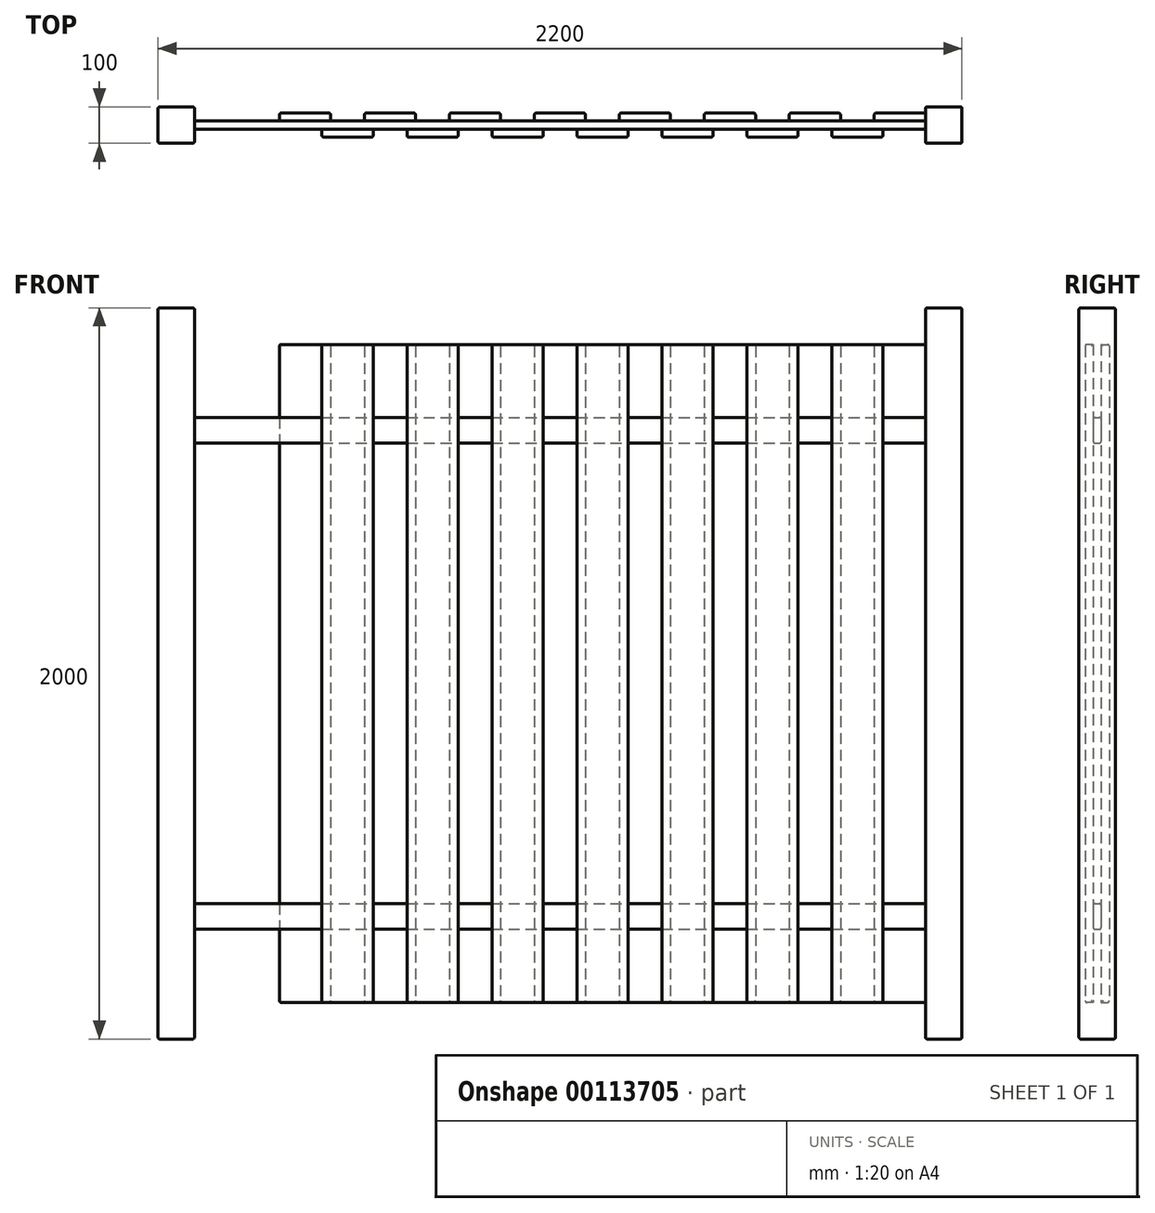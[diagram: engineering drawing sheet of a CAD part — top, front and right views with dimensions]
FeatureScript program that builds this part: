
annotation { "Feature Type Name" : "Feature", "Feature Type Description" : "" }
export const myFeature = defineFeature(function(context is Context, id is Id, definition is map)
    precondition{}
    {
        {
            var Q0;
            Q0=qCreatedBy(makeId("Top.planeOp"),FACE);
            var sketch = newSketch(context, id + "F0", { "sketchPlane" : qUnion([Q0])});
            skLineSegment(sketch, "E0.bottom", {"start": v(0, 0) * mm, "end": v(2000, 0) * mm});
            skLineSegment(sketch, "E0.top", {"start": v(0, 22) * mm, "end": v(2000, 22) * mm});
            skLineSegment(sketch, "E0.left", {"start": v(0, 0) * mm, "end": v(0, 22) * mm});
            skLineSegment(sketch, "E0.right", {"start": v(2000, 0) * mm, "end": v(2000, 22) * mm});
            skLineSegment(sketch, "E1.bottom", {"start": v(0, 22) * mm, "end": v(140, 22) * mm});
            skLineSegment(sketch, "E1.top", {"start": v(0, 44) * mm, "end": v(140, 44) * mm});
            skLineSegment(sketch, "E1.left", {"start": v(0, 22) * mm, "end": v(0, 44) * mm});
            skLineSegment(sketch, "E1.right", {"start": v(140, 22) * mm, "end": v(140, 44) * mm});
            skLineSegment(sketch, "E2.1.0.0", {"start": v(232.5, 44) * mm, "end": v(372.5, 44) * mm});
            skLineSegment(sketch, "E2.1.0.1", {"start": v(232.5, 22) * mm, "end": v(372.5, 22) * mm});
            skLineSegment(sketch, "E2.1.0.2", {"start": v(232.5, 22) * mm, "end": v(232.5, 44) * mm});
            skLineSegment(sketch, "E2.1.0.3", {"start": v(372.5, 22) * mm, "end": v(372.5, 44) * mm});
            skLineSegment(sketch, "E2.2.0.0", {"start": v(465, 44) * mm, "end": v(605, 44) * mm});
            skLineSegment(sketch, "E2.2.0.1", {"start": v(465, 22) * mm, "end": v(605, 22) * mm});
            skLineSegment(sketch, "E2.2.0.2", {"start": v(465, 22) * mm, "end": v(465, 44) * mm});
            skLineSegment(sketch, "E2.2.0.3", {"start": v(605, 22) * mm, "end": v(605, 44) * mm});
            skLineSegment(sketch, "E2.3.0.0", {"start": v(697.5, 44) * mm, "end": v(837.5, 44) * mm});
            skLineSegment(sketch, "E2.3.0.1", {"start": v(697.5, 22) * mm, "end": v(837.5, 22) * mm});
            skLineSegment(sketch, "E2.3.0.2", {"start": v(697.5, 22) * mm, "end": v(697.5, 44) * mm});
            skLineSegment(sketch, "E2.3.0.3", {"start": v(837.5, 22) * mm, "end": v(837.5, 44) * mm});
            skLineSegment(sketch, "E2.4.0.0", {"start": v(930, 44) * mm, "end": v(1070, 44) * mm});
            skLineSegment(sketch, "E2.4.0.1", {"start": v(930, 22) * mm, "end": v(1070, 22) * mm});
            skLineSegment(sketch, "E2.4.0.2", {"start": v(930, 22) * mm, "end": v(930, 44) * mm});
            skLineSegment(sketch, "E2.4.0.3", {"start": v(1070, 22) * mm, "end": v(1070, 44) * mm});
            skLineSegment(sketch, "E2.5.0.0", {"start": v(1162.5, 44) * mm, "end": v(1302.5, 44) * mm});
            skLineSegment(sketch, "E2.5.0.1", {"start": v(1162.5, 22) * mm, "end": v(1302.5, 22) * mm});
            skLineSegment(sketch, "E2.5.0.2", {"start": v(1162.5, 22) * mm, "end": v(1162.5, 44) * mm});
            skLineSegment(sketch, "E2.5.0.3", {"start": v(1302.5, 22) * mm, "end": v(1302.5, 44) * mm});
            skLineSegment(sketch, "E2.6.0.0", {"start": v(1395, 44) * mm, "end": v(1535, 44) * mm});
            skLineSegment(sketch, "E2.6.0.1", {"start": v(1395, 22) * mm, "end": v(1535, 22) * mm});
            skLineSegment(sketch, "E2.6.0.2", {"start": v(1395, 22) * mm, "end": v(1395, 44) * mm});
            skLineSegment(sketch, "E2.6.0.3", {"start": v(1535, 22) * mm, "end": v(1535, 44) * mm});
            skLineSegment(sketch, "E2.7.0.0", {"start": v(1627.5, 44) * mm, "end": v(1767.5, 44) * mm});
            skLineSegment(sketch, "E2.7.0.1", {"start": v(1627.5, 22) * mm, "end": v(1767.5, 22) * mm});
            skLineSegment(sketch, "E2.7.0.2", {"start": v(1627.5, 22) * mm, "end": v(1627.5, 44) * mm});
            skLineSegment(sketch, "E2.7.0.3", {"start": v(1767.5, 22) * mm, "end": v(1767.5, 44) * mm});
            skLineSegment(sketch, "E2.direction1", {"start": v(0, 22) * mm, "end": v(232.5, 22) * mm, "construction": true});
            skLineSegment(sketch, "E3.0.8.0", {"start": v(1860, 44) * mm, "end": v(2000, 44) * mm});
            skLineSegment(sketch, "E3.3.8.0", {"start": v(1860, 22) * mm, "end": v(2000, 22) * mm});
            skLineSegment(sketch, "E3.6.8.0", {"start": v(1860, 22) * mm, "end": v(1860, 44) * mm});
            skLineSegment(sketch, "E3.9.8.0", {"start": v(2000, 22) * mm, "end": v(2000, 44) * mm});
            skLineSegment(sketch, "E4.bottom", {"start": v(116.25, 0) * mm, "end": v(256.25, 0) * mm});
            skLineSegment(sketch, "E4.top", {"start": v(116.25, -22) * mm, "end": v(256.25, -22) * mm});
            skLineSegment(sketch, "E4.left", {"start": v(116.25, 0) * mm, "end": v(116.25, -22) * mm});
            skLineSegment(sketch, "E4.right", {"start": v(256.25, 0) * mm, "end": v(256.25, -22) * mm});
            skLineSegment(sketch, "E5.1.0.0", {"start": v(488.75, 0) * mm, "end": v(488.75, -22) * mm});
            skLineSegment(sketch, "E5.1.0.1", {"start": v(348.75, 0) * mm, "end": v(488.75, 0) * mm});
            skLineSegment(sketch, "E5.1.0.2", {"start": v(348.75, 0) * mm, "end": v(348.75, -22) * mm});
            skLineSegment(sketch, "E5.1.0.3", {"start": v(348.75, -22) * mm, "end": v(488.75, -22) * mm});
            skLineSegment(sketch, "E5.2.0.0", {"start": v(721.25, 0) * mm, "end": v(721.25, -22) * mm});
            skLineSegment(sketch, "E5.2.0.1", {"start": v(581.25, 0) * mm, "end": v(721.25, 0) * mm});
            skLineSegment(sketch, "E5.2.0.2", {"start": v(581.25, 0) * mm, "end": v(581.25, -22) * mm});
            skLineSegment(sketch, "E5.2.0.3", {"start": v(581.25, -22) * mm, "end": v(721.25, -22) * mm});
            skLineSegment(sketch, "E5.3.0.0", {"start": v(953.75, 0) * mm, "end": v(953.75, -22) * mm});
            skLineSegment(sketch, "E5.3.0.1", {"start": v(813.75, 0) * mm, "end": v(953.75, 0) * mm});
            skLineSegment(sketch, "E5.3.0.2", {"start": v(813.75, 0) * mm, "end": v(813.75, -22) * mm});
            skLineSegment(sketch, "E5.3.0.3", {"start": v(813.75, -22) * mm, "end": v(953.75, -22) * mm});
            skLineSegment(sketch, "E5.4.0.0", {"start": v(1186.25, 0) * mm, "end": v(1186.25, -22) * mm});
            skLineSegment(sketch, "E5.4.0.1", {"start": v(1046.25, 0) * mm, "end": v(1186.25, 0) * mm});
            skLineSegment(sketch, "E5.4.0.2", {"start": v(1046.25, 0) * mm, "end": v(1046.25, -22) * mm});
            skLineSegment(sketch, "E5.4.0.3", {"start": v(1046.25, -22) * mm, "end": v(1186.25, -22) * mm});
            skLineSegment(sketch, "E5.5.0.0", {"start": v(1418.75, 0) * mm, "end": v(1418.75, -22) * mm});
            skLineSegment(sketch, "E5.5.0.1", {"start": v(1278.75, 0) * mm, "end": v(1418.75, 0) * mm});
            skLineSegment(sketch, "E5.5.0.2", {"start": v(1278.75, 0) * mm, "end": v(1278.75, -22) * mm});
            skLineSegment(sketch, "E5.5.0.3", {"start": v(1278.75, -22) * mm, "end": v(1418.75, -22) * mm});
            skLineSegment(sketch, "E5.6.0.0", {"start": v(1651.25, 0) * mm, "end": v(1651.25, -22) * mm});
            skLineSegment(sketch, "E5.6.0.1", {"start": v(1511.25, 0) * mm, "end": v(1651.25, 0) * mm});
            skLineSegment(sketch, "E5.6.0.2", {"start": v(1511.25, 0) * mm, "end": v(1511.25, -22) * mm});
            skLineSegment(sketch, "E5.6.0.3", {"start": v(1511.25, -22) * mm, "end": v(1651.25, -22) * mm});
            skLineSegment(sketch, "E5.7.0.0", {"start": v(1883.75, 0) * mm, "end": v(1883.75, -22) * mm});
            skLineSegment(sketch, "E5.7.0.1", {"start": v(1743.75, 0) * mm, "end": v(1883.75, 0) * mm});
            skLineSegment(sketch, "E5.7.0.2", {"start": v(1743.75, 0) * mm, "end": v(1743.75, -22) * mm});
            skLineSegment(sketch, "E5.7.0.3", {"start": v(1743.75, -22) * mm, "end": v(1883.75, -22) * mm});
            skLineSegment(sketch, "E5.direction1", {"start": v(116.25, -22) * mm, "end": v(348.75, -22) * mm, "construction": true});
            skSolve(sketch);
        }
        {
            var Q0;
            Q0=makeQuery(id+"F0.imprint","IMPRINT",FACE,{"disambiguationData":[TD([[makeQuery(id+"F0.imprint","IMPRINT",EDGE,{"derivedFrom":sQuery(id+"F0.wireOp",EDGE,"E1.bottom")}),1.0]])]});
            var Q1;
            Q1=makeQuery(id+"F0.imprint","IMPRINT",FACE,{"disambiguationData":[TD([[makeQuery(id+"F0.imprint","IMPRINT",EDGE,{"derivedFrom":sQuery(id+"F0.wireOp",EDGE,"E2.1.0.0")}),-1.0]])]});
            var Q2;
            Q2=makeQuery(id+"F0.imprint","IMPRINT",FACE,{"disambiguationData":[TD([[makeQuery(id+"F0.imprint","IMPRINT",EDGE,{"derivedFrom":sQuery(id+"F0.wireOp",EDGE,"E2.2.0.0")}),-1.0]])]});
            var Q3;
            Q3=makeQuery(id+"F0.imprint","IMPRINT",FACE,{"disambiguationData":[TD([[makeQuery(id+"F0.imprint","IMPRINT",EDGE,{"derivedFrom":sQuery(id+"F0.wireOp",EDGE,"E2.3.0.0")}),-1.0]])]});
            var Q4;
            Q4=makeQuery(id+"F0.imprint","IMPRINT",FACE,{"disambiguationData":[TD([[makeQuery(id+"F0.imprint","IMPRINT",EDGE,{"derivedFrom":sQuery(id+"F0.wireOp",EDGE,"E2.4.0.0")}),-1.0]])]});
            var Q5;
            Q5=makeQuery(id+"F0.imprint","IMPRINT",FACE,{"disambiguationData":[TD([[makeQuery(id+"F0.imprint","IMPRINT",EDGE,{"derivedFrom":sQuery(id+"F0.wireOp",EDGE,"E2.5.0.0")}),-1.0]])]});
            var Q6;
            Q6=makeQuery(id+"F0.imprint","IMPRINT",FACE,{"disambiguationData":[TD([[makeQuery(id+"F0.imprint","IMPRINT",EDGE,{"derivedFrom":sQuery(id+"F0.wireOp",EDGE,"E2.6.0.0")}),-1.0]])]});
            var Q7;
            Q7=makeQuery(id+"F0.imprint","IMPRINT",FACE,{"disambiguationData":[TD([[makeQuery(id+"F0.imprint","IMPRINT",EDGE,{"derivedFrom":sQuery(id+"F0.wireOp",EDGE,"E2.7.0.0")}),-1.0]])]});
            var Q8;
            Q8=makeQuery(id+"F0.imprint","IMPRINT",FACE,{"disambiguationData":[TD([[makeQuery(id+"F0.imprint","IMPRINT",EDGE,{"derivedFrom":sQuery(id+"F0.wireOp",EDGE,"E3.0.8.0")}),-1.0]])]});
            var Q9;
            Q9=makeQuery(id+"F0.imprint","IMPRINT",FACE,{"disambiguationData":[TD([[makeQuery(id+"F0.imprint","IMPRINT",EDGE,{"derivedFrom":sQuery(id+"F0.wireOp",EDGE,"E5.7.0.0")}),-1.0]])]});
            var Q10;
            Q10=makeQuery(id+"F0.imprint","IMPRINT",FACE,{"disambiguationData":[TD([[makeQuery(id+"F0.imprint","IMPRINT",EDGE,{"derivedFrom":sQuery(id+"F0.wireOp",EDGE,"E5.6.0.0")}),-1.0]])]});
            var Q11;
            Q11=makeQuery(id+"F0.imprint","IMPRINT",FACE,{"disambiguationData":[TD([[makeQuery(id+"F0.imprint","IMPRINT",EDGE,{"derivedFrom":sQuery(id+"F0.wireOp",EDGE,"E5.5.0.0")}),-1.0]])]});
            var Q12;
            Q12=makeQuery(id+"F0.imprint","IMPRINT",FACE,{"disambiguationData":[TD([[makeQuery(id+"F0.imprint","IMPRINT",EDGE,{"derivedFrom":sQuery(id+"F0.wireOp",EDGE,"E5.4.0.0")}),-1.0]])]});
            var Q13;
            Q13=makeQuery(id+"F0.imprint","IMPRINT",FACE,{"disambiguationData":[TD([[makeQuery(id+"F0.imprint","IMPRINT",EDGE,{"derivedFrom":sQuery(id+"F0.wireOp",EDGE,"E5.3.0.0")}),-1.0]])]});
            var Q14;
            Q14=makeQuery(id+"F0.imprint","IMPRINT",FACE,{"disambiguationData":[TD([[makeQuery(id+"F0.imprint","IMPRINT",EDGE,{"derivedFrom":sQuery(id+"F0.wireOp",EDGE,"E5.2.0.0")}),-1.0]])]});
            var Q15;
            Q15=makeQuery(id+"F0.imprint","IMPRINT",FACE,{"disambiguationData":[TD([[makeQuery(id+"F0.imprint","IMPRINT",EDGE,{"derivedFrom":sQuery(id+"F0.wireOp",EDGE,"E5.1.0.0")}),-1.0]])]});
            var Q16;
            Q16=makeQuery(id+"F0.imprint","IMPRINT",FACE,{"disambiguationData":[TD([[makeQuery(id+"F0.imprint","IMPRINT",EDGE,{"derivedFrom":sQuery(id+"F0.wireOp",EDGE,"E4.bottom")}),-1.0]])]});
            extrude(context, id + "F1", {"entities" : qUnion([Q0, Q1, Q2, Q3, Q4, Q5, Q6, Q7, Q8, Q9, Q10, Q11, Q12, Q13, Q14, Q15, Q16]), "depth" : 1800 * mm});
        }
        {
            var Q0;
            Q0=makeQuery(id+"F1.opExtrude","SWEPT_FACE",FACE,{"disambiguationData":[OSD([sQuery(id+"F0.wireOp",EDGE,"E3.9.8.0")])]});
            var sketch = newSketch(context, id + "F2", { "sketchPlane" : qUnion([Q0])});
            skLineSegment(sketch, "E6.bottom", {"start": v(0, 270) * mm, "end": v(22, 270) * mm});
            skLineSegment(sketch, "E6.top", {"start": v(0, 200) * mm, "end": v(22, 200) * mm});
            skLineSegment(sketch, "E6.left", {"start": v(0, 270) * mm, "end": v(0, 200) * mm});
            skLineSegment(sketch, "E6.right", {"start": v(22, 270) * mm, "end": v(22, 200) * mm});
            skLineSegment(sketch, "E7.bottom", {"start": v(0, 1600) * mm, "end": v(22, 1600) * mm});
            skLineSegment(sketch, "E7.top", {"start": v(0, 1530) * mm, "end": v(22, 1530) * mm});
            skLineSegment(sketch, "E7.left", {"start": v(0, 1600) * mm, "end": v(0, 1530) * mm});
            skLineSegment(sketch, "E7.right", {"start": v(22, 1600) * mm, "end": v(22, 1530) * mm});
            skSolve(sketch);
        }
        {
            var Q0;
            Q0 = qSketchRegion(id + "F2", true);
            extrude(context, id + "F3", {"entities" : qUnion([Q0]), "oppositeDirection" : true, "depth" : 2000 * mm});
        }
        {
            var Q0;
            Q0=qCreatedBy(makeId("Top.planeOp"),FACE);
            var sketch = newSketch(context, id + "F4", { "sketchPlane" : qUnion([Q0])});
            skLineSegment(sketch, "E8.bottom", {"start": v(-100, 61) * mm, "end": v(0, 61) * mm});
            skLineSegment(sketch, "E8.top", {"start": v(-100, -39) * mm, "end": v(0, -39) * mm});
            skLineSegment(sketch, "E8.left", {"start": v(-100, 61) * mm, "end": v(-100, -39) * mm});
            skLineSegment(sketch, "E8.right", {"start": v(0, 61) * mm, "end": v(0, -39) * mm});
            skLineSegment(sketch, "E9.bottom", {"start": v(2000, 61) * mm, "end": v(2100, 61) * mm});
            skLineSegment(sketch, "E9.top", {"start": v(2000, -39) * mm, "end": v(2100, -39) * mm});
            skLineSegment(sketch, "E9.left", {"start": v(2000, 61) * mm, "end": v(2000, -39) * mm});
            skLineSegment(sketch, "E9.right", {"start": v(2100, 61) * mm, "end": v(2100, -39) * mm});
            skSolve(sketch);
        }
        {
            var Q0;
            Q0=makeQuery(id+"F4.imprint","IMPRINT",FACE,{"disambiguationData":[TD([[makeQuery(id+"F4.imprint","IMPRINT",EDGE,{"derivedFrom":sQuery(id+"F4.wireOp",EDGE,"E8.bottom")}),-1.0]])]});
            var Q1;
            Q1=makeQuery(id+"F4.imprint","IMPRINT",FACE,{"disambiguationData":[TD([[makeQuery(id+"F4.imprint","IMPRINT",EDGE,{"derivedFrom":sQuery(id+"F4.wireOp",EDGE,"E9.bottom")}),-1.0]])]});
            extrude(context, id + "F5", {"entities" : qUnion([Q0, Q1]), "depth" : 1900 * mm, "hasSecondDirection" : true, "secondDirectionOppositeDirection" : true, "secondDirectionDepth" : 100 * mm});
        }
        {
            var Q0;
            Q0=makeQuery(id+"F5.opExtrude","SWEPT_FACE",FACE,{"disambiguationData":[OSD([sQuery(id+"F4.wireOp",EDGE,"E8.top")])]});
            var Q1;
            Q1=makeQuery(id+"F1.opExtrude","SWEPT_EDGE",EDGE,{"disambiguationData":[OSD([sQuery(id+"F0.wireOp",EDGE,"E0.left"),sQuery(id+"F0.wireOp",EDGE,"E1.bottom"),sQuery(id+"F0.wireOp",EDGE,"E1.left")])]});
            var Q2;
            Q2=makeQuery(id+"F1.opExtrude","SWEPT_EDGE",EDGE,{"disambiguationData":[OSD([sQuery(id+"F0.wireOp",EDGE,"E4.top"),sQuery(id+"F0.wireOp",EDGE,"E4.right")])]});
            var Q3;
            Q3=makeQuery(id+"F1.opExtrude","SWEPT_EDGE",EDGE,{"disambiguationData":[OSD([sQuery(id+"F0.wireOp",EDGE,"E4.top"),sQuery(id+"F0.wireOp",EDGE,"E4.left")])]});
            var Q4;
            Q4=makeQuery(id+"F1.opExtrude","SWEPT_EDGE",EDGE,{"disambiguationData":[OSD([sQuery(id+"F0.wireOp",EDGE,"E0.bottom"),sQuery(id+"F0.wireOp",EDGE,"E4.bottom"),sQuery(id+"F0.wireOp",EDGE,"E4.right")])]});
            var Q5;
            Q5=makeQuery(id+"F1.opExtrude","SWEPT_EDGE",EDGE,{"disambiguationData":[OSD([sQuery(id+"F0.wireOp",EDGE,"E5.1.0.2"),sQuery(id+"F0.wireOp",EDGE,"E5.1.0.3")])]});
            var Q6;
            Q6=makeQuery(id+"F1.opExtrude","SWEPT_EDGE",EDGE,{"disambiguationData":[OSD([sQuery(id+"F0.wireOp",EDGE,"E0.bottom"),sQuery(id+"F0.wireOp",EDGE,"E5.1.0.0"),sQuery(id+"F0.wireOp",EDGE,"E5.1.0.1")])]});
            var Q7;
            Q7=makeQuery(id+"F1.opExtrude","SWEPT_EDGE",EDGE,{"disambiguationData":[OSD([sQuery(id+"F0.wireOp",EDGE,"E5.1.0.0"),sQuery(id+"F0.wireOp",EDGE,"E5.1.0.3")])]});
            var Q8;
            Q8=makeQuery(id+"F1.opExtrude","SWEPT_EDGE",EDGE,{"disambiguationData":[OSD([sQuery(id+"F0.wireOp",EDGE,"E5.2.0.2"),sQuery(id+"F0.wireOp",EDGE,"E5.2.0.3")])]});
            var Q9;
            Q9=makeQuery(id+"F1.opExtrude","SWEPT_EDGE",EDGE,{"disambiguationData":[OSD([sQuery(id+"F0.wireOp",EDGE,"E0.bottom"),sQuery(id+"F0.wireOp",EDGE,"E5.2.0.0"),sQuery(id+"F0.wireOp",EDGE,"E5.2.0.1")])]});
            var Q10;
            Q10=makeQuery(id+"F1.opExtrude","SWEPT_EDGE",EDGE,{"disambiguationData":[OSD([sQuery(id+"F0.wireOp",EDGE,"E5.2.0.0"),sQuery(id+"F0.wireOp",EDGE,"E5.2.0.3")])]});
            var Q11;
            Q11=makeQuery(id+"F1.opExtrude","CAP_EDGE",EDGE,{"disambiguationData":[OSD([sQuery(id+"F0.wireOp",EDGE,"E5.2.0.3")])],"isStart":true});
            var Q12;
            Q12=makeQuery(id+"F1.opExtrude","SWEPT_EDGE",EDGE,{"disambiguationData":[OSD([sQuery(id+"F0.wireOp",EDGE,"E0.bottom"),sQuery(id+"F0.wireOp",EDGE,"E5.3.0.0"),sQuery(id+"F0.wireOp",EDGE,"E5.3.0.1")])]});
            var Q13;
            Q13=makeQuery(id+"F1.opExtrude","CAP_EDGE",EDGE,{"disambiguationData":[OSD([sQuery(id+"F0.wireOp",EDGE,"E5.3.0.3")])],"isStart":false});
            var Q14;
            Q14=makeQuery(id+"F1.opExtrude","SWEPT_EDGE",EDGE,{"disambiguationData":[OSD([sQuery(id+"F0.wireOp",EDGE,"E5.3.0.0"),sQuery(id+"F0.wireOp",EDGE,"E5.3.0.3")])]});
            var Q15;
            Q15=makeQuery(id+"F1.opExtrude","SWEPT_EDGE",EDGE,{"disambiguationData":[OSD([sQuery(id+"F0.wireOp",EDGE,"E5.3.0.2"),sQuery(id+"F0.wireOp",EDGE,"E5.3.0.3")])]});
            var Q16;
            Q16=makeQuery(id+"F1.opExtrude","SWEPT_EDGE",EDGE,{"disambiguationData":[OSD([sQuery(id+"F0.wireOp",EDGE,"E5.4.0.2"),sQuery(id+"F0.wireOp",EDGE,"E5.4.0.3")])]});
            var Q17;
            Q17=makeQuery(id+"F1.opExtrude","SWEPT_EDGE",EDGE,{"disambiguationData":[OSD([sQuery(id+"F0.wireOp",EDGE,"E5.4.0.0"),sQuery(id+"F0.wireOp",EDGE,"E5.4.0.3")])]});
            var Q18;
            Q18=makeQuery(id+"F1.opExtrude","SWEPT_EDGE",EDGE,{"disambiguationData":[OSD([sQuery(id+"F0.wireOp",EDGE,"E0.bottom"),sQuery(id+"F0.wireOp",EDGE,"E5.4.0.0"),sQuery(id+"F0.wireOp",EDGE,"E5.4.0.1")])]});
            var Q19;
            Q19=makeQuery(id+"F1.opExtrude","CAP_EDGE",EDGE,{"disambiguationData":[OSD([sQuery(id+"F0.wireOp",EDGE,"E5.5.0.3")])],"isStart":false});
            var Q20;
            Q20=makeQuery(id+"F1.opExtrude","SWEPT_EDGE",EDGE,{"disambiguationData":[OSD([sQuery(id+"F0.wireOp",EDGE,"E5.5.0.2"),sQuery(id+"F0.wireOp",EDGE,"E5.5.0.3")])]});
            var Q21;
            Q21=makeQuery(id+"F1.opExtrude","SWEPT_EDGE",EDGE,{"disambiguationData":[OSD([sQuery(id+"F0.wireOp",EDGE,"E0.bottom"),sQuery(id+"F0.wireOp",EDGE,"E5.5.0.0"),sQuery(id+"F0.wireOp",EDGE,"E5.5.0.1")])]});
            var Q22;
            Q22=makeQuery(id+"F1.opExtrude","SWEPT_EDGE",EDGE,{"disambiguationData":[OSD([sQuery(id+"F0.wireOp",EDGE,"E5.5.0.0"),sQuery(id+"F0.wireOp",EDGE,"E5.5.0.3")])]});
            var Q23;
            Q23=makeQuery(id+"F1.opExtrude","CAP_EDGE",EDGE,{"disambiguationData":[OSD([sQuery(id+"F0.wireOp",EDGE,"E5.5.0.3")])],"isStart":true});
            var Q24;
            Q24=makeQuery(id+"F1.opExtrude","SWEPT_EDGE",EDGE,{"disambiguationData":[OSD([sQuery(id+"F0.wireOp",EDGE,"E5.6.0.2"),sQuery(id+"F0.wireOp",EDGE,"E5.6.0.3")])]});
            var Q25;
            Q25=makeQuery(id+"F1.opExtrude","SWEPT_EDGE",EDGE,{"disambiguationData":[OSD([sQuery(id+"F0.wireOp",EDGE,"E0.bottom"),sQuery(id+"F0.wireOp",EDGE,"E5.6.0.0"),sQuery(id+"F0.wireOp",EDGE,"E5.6.0.1")])]});
            var Q26;
            Q26=makeQuery(id+"F1.opExtrude","SWEPT_EDGE",EDGE,{"disambiguationData":[OSD([sQuery(id+"F0.wireOp",EDGE,"E5.6.0.0"),sQuery(id+"F0.wireOp",EDGE,"E5.6.0.3")])]});
            var Q27;
            Q27=makeQuery(id+"F1.opExtrude","SWEPT_EDGE",EDGE,{"disambiguationData":[OSD([sQuery(id+"F0.wireOp",EDGE,"E0.bottom"),sQuery(id+"F0.wireOp",EDGE,"E5.7.0.0"),sQuery(id+"F0.wireOp",EDGE,"E5.7.0.1")])]});
            var Q28;
            Q28=makeQuery(id+"F1.opExtrude","CAP_EDGE",EDGE,{"disambiguationData":[OSD([sQuery(id+"F0.wireOp",EDGE,"E5.7.0.3")])],"isStart":false});
            var Q29;
            Q29=makeQuery(id+"F1.opExtrude","SWEPT_EDGE",EDGE,{"disambiguationData":[OSD([sQuery(id+"F0.wireOp",EDGE,"E5.7.0.0"),sQuery(id+"F0.wireOp",EDGE,"E5.7.0.3")])]});
            var Q30;
            Q30=makeQuery(id+"F1.opExtrude","CAP_EDGE",EDGE,{"disambiguationData":[OSD([sQuery(id+"F0.wireOp",EDGE,"E5.7.0.3")])],"isStart":true});
            var Q31;
            Q31=makeQuery(id+"F1.opExtrude","SWEPT_EDGE",EDGE,{"disambiguationData":[OSD([sQuery(id+"F0.wireOp",EDGE,"E5.7.0.2"),sQuery(id+"F0.wireOp",EDGE,"E5.7.0.3")])]});
            var Q32;
            Q32=makeQuery(id+"F3.opExtrude","SWEPT_EDGE",EDGE,{"disambiguationData":[OSD([sQuery(id+"F2.wireOp",EDGE,"E6.top"),sQuery(id+"F2.wireOp",EDGE,"E6.left")])]});
            var Q33;
            Q33=makeQuery(id+"F3.opExtrude","SWEPT_EDGE",EDGE,{"disambiguationData":[OSD([sQuery(id+"F0.wireOp",EDGE,"E0.right"),sQuery(id+"F0.wireOp",EDGE,"E3.3.8.0"),sQuery(id+"F0.wireOp",EDGE,"E3.9.8.0"),sQuery(id+"F2.wireOp",EDGE,"E6.bottom"),sQuery(id+"F2.wireOp",EDGE,"E6.right")])]});
            var Q34;
            Q34=makeQuery(id+"F3.opExtrude","SWEPT_EDGE",EDGE,{"disambiguationData":[OSD([sQuery(id+"F2.wireOp",EDGE,"E6.bottom"),sQuery(id+"F2.wireOp",EDGE,"E6.left")])]});
            var Q35;
            Q35=makeQuery(id+"F3.opExtrude","SWEPT_EDGE",EDGE,{"disambiguationData":[OSD([sQuery(id+"F2.wireOp",EDGE,"E7.top"),sQuery(id+"F2.wireOp",EDGE,"E7.left")])]});
            var Q36;
            Q36=makeQuery(id+"F3.opExtrude","SWEPT_EDGE",EDGE,{"disambiguationData":[OSD([sQuery(id+"F0.wireOp",EDGE,"E0.right"),sQuery(id+"F0.wireOp",EDGE,"E3.3.8.0"),sQuery(id+"F0.wireOp",EDGE,"E3.9.8.0"),sQuery(id+"F2.wireOp",EDGE,"E7.bottom"),sQuery(id+"F2.wireOp",EDGE,"E7.right")])]});
            var Q37;
            Q37=makeQuery(id+"F3.opExtrude","SWEPT_EDGE",EDGE,{"disambiguationData":[OSD([sQuery(id+"F2.wireOp",EDGE,"E7.bottom"),sQuery(id+"F2.wireOp",EDGE,"E7.left")])]});
            var Q38;
            Q38=makeQuery(id+"F5.opExtrude","CAP_EDGE",EDGE,{"disambiguationData":[OSD([sQuery(id+"F4.wireOp",EDGE,"E8.top")])],"isStart":false});
            var Q39;
            Q39=makeQuery(id+"F5.opExtrude","SWEPT_EDGE",EDGE,{"disambiguationData":[OSD([sQuery(id+"F4.wireOp",EDGE,"E8.top"),sQuery(id+"F4.wireOp",EDGE,"E8.right")])]});
            var Q40;
            Q40=makeQuery(id+"F5.opExtrude","SWEPT_EDGE",EDGE,{"disambiguationData":[OSD([sQuery(id+"F4.wireOp",EDGE,"E8.top"),sQuery(id+"F4.wireOp",EDGE,"E8.left")])]});
            var Q41;
            Q41=makeQuery(id+"F5.opExtrude","SWEPT_EDGE",EDGE,{"disambiguationData":[OSD([sQuery(id+"F4.wireOp",EDGE,"E9.top"),sQuery(id+"F4.wireOp",EDGE,"E9.right")])]});
            var Q42;
            Q42=makeQuery(id+"F5.opExtrude","SWEPT_EDGE",EDGE,{"disambiguationData":[OSD([sQuery(id+"F4.wireOp",EDGE,"E9.top"),sQuery(id+"F4.wireOp",EDGE,"E9.left")])]});
            var Q43;
            Q43=makeQuery(id+"F5.opExtrude","SWEPT_EDGE",EDGE,{"disambiguationData":[OSD([sQuery(id+"F4.wireOp",EDGE,"E9.bottom"),sQuery(id+"F4.wireOp",EDGE,"E9.right")])]});
            var Q44;
            Q44=makeQuery(id+"F1.opExtrude","CAP_EDGE",EDGE,{"disambiguationData":[OSD([sQuery(id+"F0.wireOp",EDGE,"E1.bottom")])],"isStart":false});
            var Q45;
            Q45=makeQuery(id+"F1.opExtrude","SWEPT_EDGE",EDGE,{"disambiguationData":[OSD([sQuery(id+"F0.wireOp",EDGE,"E1.top"),sQuery(id+"F0.wireOp",EDGE,"E1.left")])]});
            var Q46;
            Q46=makeQuery(id+"F1.opExtrude","CAP_EDGE",EDGE,{"disambiguationData":[OSD([sQuery(id+"F0.wireOp",EDGE,"E2.5.0.1")])],"isStart":true});
            var Q47;
            Q47=makeQuery(id+"F1.opExtrude","CAP_EDGE",EDGE,{"disambiguationData":[OSD([sQuery(id+"F0.wireOp",EDGE,"E2.7.0.1")])],"isStart":true});
            var Q48;
            Q48=makeQuery(id+"F1.opExtrude","CAP_EDGE",EDGE,{"disambiguationData":[OSD([sQuery(id+"F0.wireOp",EDGE,"E3.3.8.0")])],"isStart":true});
            var Q49;
            Q49=makeQuery(id+"F1.opExtrude","CAP_EDGE",EDGE,{"disambiguationData":[OSD([sQuery(id+"F0.wireOp",EDGE,"E3.3.8.0")])],"isStart":false});
            var Q50;
            Q50=makeQuery(id+"F1.opExtrude","CAP_EDGE",EDGE,{"disambiguationData":[OSD([sQuery(id+"F0.wireOp",EDGE,"E3.9.8.0")])],"isStart":false});
            var Q51;
            Q51=makeQuery(id+"F1.opExtrude","SWEPT_EDGE",EDGE,{"disambiguationData":[OSD([sQuery(id+"F0.wireOp",EDGE,"E0.right"),sQuery(id+"F0.wireOp",EDGE,"E3.3.8.0"),sQuery(id+"F0.wireOp",EDGE,"E3.9.8.0")])]});
            var Q52;
            Q52=makeQuery(id+"F1.opExtrude","SWEPT_EDGE",EDGE,{"disambiguationData":[OSD([sQuery(id+"F0.wireOp",EDGE,"E3.0.8.0"),sQuery(id+"F0.wireOp",EDGE,"E3.9.8.0")])]});
            var Q53;
            Q53=makeQuery(id+"F1.opExtrude","CAP_EDGE",EDGE,{"disambiguationData":[OSD([sQuery(id+"F0.wireOp",EDGE,"E4.top")])],"isStart":true});
            var Q54;
            Q54=makeQuery(id+"F1.opExtrude","CAP_EDGE",EDGE,{"disambiguationData":[OSD([sQuery(id+"F0.wireOp",EDGE,"E4.top")])],"isStart":false});
            var Q55;
            Q55=makeQuery(id+"F1.opExtrude","SWEPT_EDGE",EDGE,{"disambiguationData":[OSD([sQuery(id+"F0.wireOp",EDGE,"E0.bottom"),sQuery(id+"F0.wireOp",EDGE,"E4.bottom"),sQuery(id+"F0.wireOp",EDGE,"E4.left")])]});
            var Q56;
            Q56=makeQuery(id+"F1.opExtrude","CAP_EDGE",EDGE,{"disambiguationData":[OSD([sQuery(id+"F0.wireOp",EDGE,"E5.1.0.0")])],"isStart":true});
            var Q57;
            Q57=makeQuery(id+"F1.opExtrude","CAP_EDGE",EDGE,{"disambiguationData":[OSD([sQuery(id+"F0.wireOp",EDGE,"E5.1.0.3")])],"isStart":false});
            var Q58;
            Q58=makeQuery(id+"F1.opExtrude","CAP_EDGE",EDGE,{"disambiguationData":[OSD([sQuery(id+"F0.wireOp",EDGE,"E5.1.0.2")])],"isStart":true});
            var Q59;
            Q59=makeQuery(id+"F1.opExtrude","SWEPT_EDGE",EDGE,{"disambiguationData":[OSD([sQuery(id+"F0.wireOp",EDGE,"E0.bottom"),sQuery(id+"F0.wireOp",EDGE,"E5.1.0.1"),sQuery(id+"F0.wireOp",EDGE,"E5.1.0.2")])]});
            var Q60;
            Q60=makeQuery(id+"F1.opExtrude","CAP_EDGE",EDGE,{"disambiguationData":[OSD([sQuery(id+"F0.wireOp",EDGE,"E5.1.0.3")])],"isStart":true});
            var Q61;
            Q61=makeQuery(id+"F1.opExtrude","CAP_EDGE",EDGE,{"disambiguationData":[OSD([sQuery(id+"F0.wireOp",EDGE,"E5.2.0.1")])],"isStart":false});
            var Q62;
            Q62=makeQuery(id+"F1.opExtrude","SWEPT_EDGE",EDGE,{"disambiguationData":[OSD([sQuery(id+"F0.wireOp",EDGE,"E0.bottom"),sQuery(id+"F0.wireOp",EDGE,"E5.2.0.1"),sQuery(id+"F0.wireOp",EDGE,"E5.2.0.2")])]});
            var Q63;
            Q63=makeQuery(id+"F1.opExtrude","CAP_EDGE",EDGE,{"disambiguationData":[OSD([sQuery(id+"F0.wireOp",EDGE,"E5.2.0.2")])],"isStart":true});
            var Q64;
            Q64=makeQuery(id+"F1.opExtrude","CAP_EDGE",EDGE,{"disambiguationData":[OSD([sQuery(id+"F0.wireOp",EDGE,"E5.2.0.0")])],"isStart":true});
            var Q65;
            Q65=makeQuery(id+"F1.opExtrude","CAP_EDGE",EDGE,{"disambiguationData":[OSD([sQuery(id+"F0.wireOp",EDGE,"E5.2.0.0")])],"isStart":false});
            var Q66;
            Q66=makeQuery(id+"F1.opExtrude","CAP_EDGE",EDGE,{"disambiguationData":[OSD([sQuery(id+"F0.wireOp",EDGE,"E5.2.0.2")])],"isStart":false});
            var Q67;
            Q67=makeQuery(id+"F1.opExtrude","CAP_EDGE",EDGE,{"disambiguationData":[OSD([sQuery(id+"F0.wireOp",EDGE,"E5.2.0.3")])],"isStart":false});
            var Q68;
            Q68=makeQuery(id+"F1.opExtrude","CAP_EDGE",EDGE,{"disambiguationData":[OSD([sQuery(id+"F0.wireOp",EDGE,"E5.3.0.0")])],"isStart":false});
            var Q69;
            Q69=makeQuery(id+"F1.opExtrude","CAP_EDGE",EDGE,{"disambiguationData":[OSD([sQuery(id+"F0.wireOp",EDGE,"E5.3.0.1")])],"isStart":true});
            var Q70;
            Q70=makeQuery(id+"F1.opExtrude","CAP_EDGE",EDGE,{"disambiguationData":[OSD([sQuery(id+"F0.wireOp",EDGE,"E5.3.0.0")])],"isStart":true});
            var Q71;
            Q71=makeQuery(id+"F1.opExtrude","CAP_EDGE",EDGE,{"disambiguationData":[OSD([sQuery(id+"F0.wireOp",EDGE,"E5.3.0.2")])],"isStart":true});
            var Q72;
            Q72=makeQuery(id+"F1.opExtrude","CAP_EDGE",EDGE,{"disambiguationData":[OSD([sQuery(id+"F0.wireOp",EDGE,"E5.3.0.2")])],"isStart":false});
            var Q73;
            Q73=makeQuery(id+"F1.opExtrude","SWEPT_EDGE",EDGE,{"disambiguationData":[OSD([sQuery(id+"F0.wireOp",EDGE,"E0.bottom"),sQuery(id+"F0.wireOp",EDGE,"E5.3.0.1"),sQuery(id+"F0.wireOp",EDGE,"E5.3.0.2")])]});
            var Q74;
            Q74=makeQuery(id+"F1.opExtrude","CAP_EDGE",EDGE,{"disambiguationData":[OSD([sQuery(id+"F0.wireOp",EDGE,"E5.3.0.3")])],"isStart":true});
            var Q75;
            Q75=makeQuery(id+"F1.opExtrude","CAP_EDGE",EDGE,{"disambiguationData":[OSD([sQuery(id+"F0.wireOp",EDGE,"E5.4.0.1")])],"isStart":true});
            var Q76;
            Q76=makeQuery(id+"F1.opExtrude","SWEPT_EDGE",EDGE,{"disambiguationData":[OSD([sQuery(id+"F0.wireOp",EDGE,"E0.bottom"),sQuery(id+"F0.wireOp",EDGE,"E5.4.0.1"),sQuery(id+"F0.wireOp",EDGE,"E5.4.0.2")])]});
            var Q77;
            Q77=makeQuery(id+"F1.opExtrude","CAP_EDGE",EDGE,{"disambiguationData":[OSD([sQuery(id+"F0.wireOp",EDGE,"E5.4.0.0")])],"isStart":true});
            var Q78;
            Q78=makeQuery(id+"F1.opExtrude","CAP_EDGE",EDGE,{"disambiguationData":[OSD([sQuery(id+"F0.wireOp",EDGE,"E5.4.0.1")])],"isStart":false});
            var Q79;
            Q79=makeQuery(id+"F1.opExtrude","CAP_EDGE",EDGE,{"disambiguationData":[OSD([sQuery(id+"F0.wireOp",EDGE,"E5.4.0.2")])],"isStart":true});
            var Q80;
            Q80=makeQuery(id+"F1.opExtrude","CAP_EDGE",EDGE,{"disambiguationData":[OSD([sQuery(id+"F0.wireOp",EDGE,"E5.4.0.0")])],"isStart":false});
            var Q81;
            Q81=makeQuery(id+"F1.opExtrude","CAP_EDGE",EDGE,{"disambiguationData":[OSD([sQuery(id+"F0.wireOp",EDGE,"E5.4.0.2")])],"isStart":false});
            var Q82;
            Q82=makeQuery(id+"F1.opExtrude","CAP_EDGE",EDGE,{"disambiguationData":[OSD([sQuery(id+"F0.wireOp",EDGE,"E5.4.0.3")])],"isStart":true});
            var Q83;
            Q83=makeQuery(id+"F1.opExtrude","CAP_EDGE",EDGE,{"disambiguationData":[OSD([sQuery(id+"F0.wireOp",EDGE,"E5.4.0.3")])],"isStart":false});
            var Q84;
            Q84=makeQuery(id+"F1.opExtrude","CAP_EDGE",EDGE,{"disambiguationData":[OSD([sQuery(id+"F0.wireOp",EDGE,"E5.5.0.0")])],"isStart":false});
            var Q85;
            Q85=makeQuery(id+"F1.opExtrude","CAP_EDGE",EDGE,{"disambiguationData":[OSD([sQuery(id+"F0.wireOp",EDGE,"E5.5.0.1")])],"isStart":true});
            var Q86;
            Q86=makeQuery(id+"F1.opExtrude","CAP_EDGE",EDGE,{"disambiguationData":[OSD([sQuery(id+"F0.wireOp",EDGE,"E5.5.0.0")])],"isStart":true});
            var Q87;
            Q87=makeQuery(id+"F1.opExtrude","CAP_EDGE",EDGE,{"disambiguationData":[OSD([sQuery(id+"F0.wireOp",EDGE,"E5.5.0.2")])],"isStart":true});
            var Q88;
            Q88=makeQuery(id+"F1.opExtrude","CAP_EDGE",EDGE,{"disambiguationData":[OSD([sQuery(id+"F0.wireOp",EDGE,"E5.5.0.2")])],"isStart":false});
            var Q89;
            Q89=makeQuery(id+"F1.opExtrude","SWEPT_EDGE",EDGE,{"disambiguationData":[OSD([sQuery(id+"F0.wireOp",EDGE,"E0.bottom"),sQuery(id+"F0.wireOp",EDGE,"E5.5.0.1"),sQuery(id+"F0.wireOp",EDGE,"E5.5.0.2")])]});
            var Q90;
            Q90=makeQuery(id+"F1.opExtrude","SWEPT_EDGE",EDGE,{"disambiguationData":[OSD([sQuery(id+"F0.wireOp",EDGE,"E0.bottom"),sQuery(id+"F0.wireOp",EDGE,"E5.6.0.1"),sQuery(id+"F0.wireOp",EDGE,"E5.6.0.2")])]});
            var Q91;
            Q91=makeQuery(id+"F1.opExtrude","CAP_EDGE",EDGE,{"disambiguationData":[OSD([sQuery(id+"F0.wireOp",EDGE,"E5.6.0.1")])],"isStart":true});
            var Q92;
            Q92=makeQuery(id+"F1.opExtrude","CAP_EDGE",EDGE,{"disambiguationData":[OSD([sQuery(id+"F0.wireOp",EDGE,"E5.6.0.0")])],"isStart":true});
            var Q93;
            Q93=makeQuery(id+"F1.opExtrude","CAP_EDGE",EDGE,{"disambiguationData":[OSD([sQuery(id+"F0.wireOp",EDGE,"E5.6.0.2")])],"isStart":true});
            var Q94;
            Q94=makeQuery(id+"F1.opExtrude","CAP_EDGE",EDGE,{"disambiguationData":[OSD([sQuery(id+"F0.wireOp",EDGE,"E5.6.0.0")])],"isStart":false});
            var Q95;
            Q95=makeQuery(id+"F1.opExtrude","CAP_EDGE",EDGE,{"disambiguationData":[OSD([sQuery(id+"F0.wireOp",EDGE,"E5.6.0.2")])],"isStart":false});
            var Q96;
            Q96=makeQuery(id+"F1.opExtrude","CAP_EDGE",EDGE,{"disambiguationData":[OSD([sQuery(id+"F0.wireOp",EDGE,"E5.6.0.3")])],"isStart":true});
            var Q97;
            Q97=makeQuery(id+"F1.opExtrude","CAP_EDGE",EDGE,{"disambiguationData":[OSD([sQuery(id+"F0.wireOp",EDGE,"E5.6.0.3")])],"isStart":false});
            var Q98;
            Q98=makeQuery(id+"F1.opExtrude","CAP_EDGE",EDGE,{"disambiguationData":[OSD([sQuery(id+"F0.wireOp",EDGE,"E5.7.0.0")])],"isStart":false});
            var Q99;
            Q99=makeQuery(id+"F1.opExtrude","CAP_EDGE",EDGE,{"disambiguationData":[OSD([sQuery(id+"F0.wireOp",EDGE,"E5.7.0.0")])],"isStart":true});
            var Q100;
            Q100=makeQuery(id+"F1.opExtrude","CAP_EDGE",EDGE,{"disambiguationData":[OSD([sQuery(id+"F0.wireOp",EDGE,"E5.7.0.2")])],"isStart":true});
            var Q101;
            Q101=makeQuery(id+"F1.opExtrude","SWEPT_EDGE",EDGE,{"disambiguationData":[OSD([sQuery(id+"F0.wireOp",EDGE,"E0.bottom"),sQuery(id+"F0.wireOp",EDGE,"E5.7.0.1"),sQuery(id+"F0.wireOp",EDGE,"E5.7.0.2")])]});
            var Q102;
            Q102=makeQuery(id+"F3.opExtrude","CAP_EDGE",EDGE,{"disambiguationData":[OSD([sQuery(id+"F2.wireOp",EDGE,"E6.left")])],"isStart":true});
            var Q103;
            Q103=makeQuery(id+"F3.opExtrude","CAP_EDGE",EDGE,{"disambiguationData":[OSD([sQuery(id+"F2.wireOp",EDGE,"E6.top")])],"isStart":true});
            var Q104;
            Q104=makeQuery(id+"F3.opExtrude","CAP_EDGE",EDGE,{"disambiguationData":[OSD([sQuery(id+"F2.wireOp",EDGE,"E6.bottom")])],"isStart":true});
            var Q105;
            Q105=makeQuery(id+"F3.opExtrude","SWEPT_EDGE",EDGE,{"disambiguationData":[OSD([sQuery(id+"F0.wireOp",EDGE,"E0.right"),sQuery(id+"F0.wireOp",EDGE,"E3.3.8.0"),sQuery(id+"F0.wireOp",EDGE,"E3.9.8.0"),sQuery(id+"F2.wireOp",EDGE,"E6.top"),sQuery(id+"F2.wireOp",EDGE,"E6.right")])]});
            var Q106;
            Q106=makeQuery(id+"F3.opExtrude","CAP_EDGE",EDGE,{"disambiguationData":[OSD([sQuery(id+"F2.wireOp",EDGE,"E6.left")])],"isStart":false});
            var Q107;
            Q107=makeQuery(id+"F3.opExtrude","SWEPT_EDGE",EDGE,{"disambiguationData":[OSD([sQuery(id+"F0.wireOp",EDGE,"E0.right"),sQuery(id+"F0.wireOp",EDGE,"E3.3.8.0"),sQuery(id+"F0.wireOp",EDGE,"E3.9.8.0"),sQuery(id+"F2.wireOp",EDGE,"E7.top"),sQuery(id+"F2.wireOp",EDGE,"E7.right")])]});
            var Q108;
            Q108=makeQuery(id+"F3.opExtrude","CAP_EDGE",EDGE,{"disambiguationData":[OSD([sQuery(id+"F2.wireOp",EDGE,"E7.left")])],"isStart":true});
            var Q109;
            Q109=makeQuery(id+"F3.opExtrude","CAP_EDGE",EDGE,{"disambiguationData":[OSD([sQuery(id+"F2.wireOp",EDGE,"E7.bottom")])],"isStart":true});
            var Q110;
            Q110=makeQuery(id+"F3.opExtrude","CAP_EDGE",EDGE,{"disambiguationData":[OSD([sQuery(id+"F2.wireOp",EDGE,"E7.top")])],"isStart":true});
            var Q111;
            Q111=makeQuery(id+"F3.opExtrude","CAP_EDGE",EDGE,{"disambiguationData":[OSD([sQuery(id+"F2.wireOp",EDGE,"E7.left")])],"isStart":false});
            var Q112;
            Q112=makeQuery(id+"F5.opExtrude","CAP_EDGE",EDGE,{"disambiguationData":[OSD([sQuery(id+"F4.wireOp",EDGE,"E8.top")])],"isStart":true});
            var Q113;
            Q113=makeQuery(id+"F5.opExtrude","CAP_EDGE",EDGE,{"disambiguationData":[OSD([sQuery(id+"F4.wireOp",EDGE,"E8.bottom")])],"isStart":false});
            var Q114;
            Q114=makeQuery(id+"F5.opExtrude","SWEPT_EDGE",EDGE,{"disambiguationData":[OSD([sQuery(id+"F4.wireOp",EDGE,"E8.bottom"),sQuery(id+"F4.wireOp",EDGE,"E8.left")])]});
            var Q115;
            Q115=makeQuery(id+"F5.opExtrude","CAP_EDGE",EDGE,{"disambiguationData":[OSD([sQuery(id+"F4.wireOp",EDGE,"E8.right")])],"isStart":false});
            var Q116;
            Q116=makeQuery(id+"F5.opExtrude","CAP_EDGE",EDGE,{"disambiguationData":[OSD([sQuery(id+"F4.wireOp",EDGE,"E8.left")])],"isStart":false});
            var Q117;
            Q117=makeQuery(id+"F5.opExtrude","CAP_EDGE",EDGE,{"disambiguationData":[OSD([sQuery(id+"F4.wireOp",EDGE,"E9.top")])],"isStart":true});
            var Q118;
            Q118=makeQuery(id+"F5.opExtrude","CAP_EDGE",EDGE,{"disambiguationData":[OSD([sQuery(id+"F4.wireOp",EDGE,"E9.right")])],"isStart":true});
            var Q119;
            Q119=makeQuery(id+"F5.opExtrude","SWEPT_EDGE",EDGE,{"disambiguationData":[OSD([sQuery(id+"F4.wireOp",EDGE,"E9.bottom"),sQuery(id+"F4.wireOp",EDGE,"E9.left")])]});
            var Q120;
            Q120=makeQuery(id+"F5.opExtrude","CAP_EDGE",EDGE,{"disambiguationData":[OSD([sQuery(id+"F4.wireOp",EDGE,"E9.bottom")])],"isStart":false});
            var Q121;
            Q121=makeQuery(id+"F5.opExtrude","CAP_EDGE",EDGE,{"disambiguationData":[OSD([sQuery(id+"F4.wireOp",EDGE,"E9.left")])],"isStart":false});
            var Q122;
            Q122=makeQuery(id+"F5.opExtrude","CAP_EDGE",EDGE,{"disambiguationData":[OSD([sQuery(id+"F4.wireOp",EDGE,"E9.right")])],"isStart":false});
            var Q123;
            Q123=makeQuery(id+"F5.opExtrude","CAP_EDGE",EDGE,{"disambiguationData":[OSD([sQuery(id+"F4.wireOp",EDGE,"E9.left")])],"isStart":true});
            var Q124;
            Q124=makeQuery(id+"F5.opExtrude","CAP_EDGE",EDGE,{"disambiguationData":[OSD([sQuery(id+"F4.wireOp",EDGE,"E9.bottom")])],"isStart":true});
            var Q125;
            Q125=makeQuery(id+"F5.opExtrude","CAP_EDGE",EDGE,{"disambiguationData":[OSD([sQuery(id+"F4.wireOp",EDGE,"E9.top")])],"isStart":false});
            var Q126;
            Q126=makeQuery(id+"F1.opExtrude","CAP_EDGE",EDGE,{"disambiguationData":[OSD([sQuery(id+"F0.wireOp",EDGE,"E2.2.0.1")])],"isStart":true});
            var Q127;
            Q127=makeQuery(id+"F1.opExtrude","CAP_EDGE",EDGE,{"disambiguationData":[OSD([sQuery(id+"F0.wireOp",EDGE,"E2.2.0.0")])],"isStart":false});
            var Q128;
            Q128=makeQuery(id+"F1.opExtrude","CAP_EDGE",EDGE,{"disambiguationData":[OSD([sQuery(id+"F0.wireOp",EDGE,"E2.2.0.3")])],"isStart":false});
            var Q129;
            Q129=makeQuery(id+"F1.opExtrude","SWEPT_EDGE",EDGE,{"disambiguationData":[OSD([sQuery(id+"F0.wireOp",EDGE,"E0.top"),sQuery(id+"F0.wireOp",EDGE,"E2.2.0.1"),sQuery(id+"F0.wireOp",EDGE,"E2.2.0.3")])]});
            var Q130;
            Q130=makeQuery(id+"F1.opExtrude","SWEPT_EDGE",EDGE,{"disambiguationData":[OSD([sQuery(id+"F0.wireOp",EDGE,"E2.2.0.0"),sQuery(id+"F0.wireOp",EDGE,"E2.2.0.2")])]});
            var Q131;
            Q131=makeQuery(id+"F1.opExtrude","SWEPT_EDGE",EDGE,{"disambiguationData":[OSD([sQuery(id+"F0.wireOp",EDGE,"E2.2.0.0"),sQuery(id+"F0.wireOp",EDGE,"E2.2.0.3")])]});
            var Q132;
            Q132=makeQuery(id+"F1.opExtrude","SWEPT_EDGE",EDGE,{"disambiguationData":[OSD([sQuery(id+"F0.wireOp",EDGE,"E0.top"),sQuery(id+"F0.wireOp",EDGE,"E2.2.0.1"),sQuery(id+"F0.wireOp",EDGE,"E2.2.0.2")])]});
            var Q133;
            Q133=makeQuery(id+"F1.opExtrude","CAP_EDGE",EDGE,{"disambiguationData":[OSD([sQuery(id+"F0.wireOp",EDGE,"E1.top")])],"isStart":false});
            var Q134;
            Q134=makeQuery(id+"F1.opExtrude","CAP_EDGE",EDGE,{"disambiguationData":[OSD([sQuery(id+"F0.wireOp",EDGE,"E1.bottom")])],"isStart":true});
            var Q135;
            Q135=makeQuery(id+"F1.opExtrude","CAP_EDGE",EDGE,{"disambiguationData":[OSD([sQuery(id+"F0.wireOp",EDGE,"E1.right")])],"isStart":false});
            var Q136;
            Q136=makeQuery(id+"F1.opExtrude","SWEPT_EDGE",EDGE,{"disambiguationData":[OSD([sQuery(id+"F0.wireOp",EDGE,"E0.top"),sQuery(id+"F0.wireOp",EDGE,"E1.bottom"),sQuery(id+"F0.wireOp",EDGE,"E1.right")])]});
            var Q137;
            Q137=makeQuery(id+"F1.opExtrude","SWEPT_EDGE",EDGE,{"disambiguationData":[OSD([sQuery(id+"F0.wireOp",EDGE,"E1.top"),sQuery(id+"F0.wireOp",EDGE,"E1.right")])]});
            var Q138;
            Q138=makeQuery(id+"F1.opExtrude","CAP_EDGE",EDGE,{"disambiguationData":[OSD([sQuery(id+"F0.wireOp",EDGE,"E1.left")])],"isStart":false});
            var Q139;
            Q139=makeQuery(id+"F1.opExtrude","CAP_EDGE",EDGE,{"disambiguationData":[OSD([sQuery(id+"F0.wireOp",EDGE,"E2.1.0.1")])],"isStart":false});
            var Q140;
            Q140=makeQuery(id+"F1.opExtrude","CAP_EDGE",EDGE,{"disambiguationData":[OSD([sQuery(id+"F0.wireOp",EDGE,"E2.1.0.0")])],"isStart":false});
            var Q141;
            Q141=makeQuery(id+"F1.opExtrude","SWEPT_EDGE",EDGE,{"disambiguationData":[OSD([sQuery(id+"F0.wireOp",EDGE,"E2.1.0.0"),sQuery(id+"F0.wireOp",EDGE,"E2.1.0.2")])]});
            var Q142;
            Q142=makeQuery(id+"F1.opExtrude","SWEPT_EDGE",EDGE,{"disambiguationData":[OSD([sQuery(id+"F0.wireOp",EDGE,"E2.1.0.0"),sQuery(id+"F0.wireOp",EDGE,"E2.1.0.3")])]});
            var Q143;
            Q143=makeQuery(id+"F1.opExtrude","SWEPT_EDGE",EDGE,{"disambiguationData":[OSD([sQuery(id+"F0.wireOp",EDGE,"E0.top"),sQuery(id+"F0.wireOp",EDGE,"E2.1.0.1"),sQuery(id+"F0.wireOp",EDGE,"E2.1.0.2")])]});
            var Q144;
            Q144=makeQuery(id+"F1.opExtrude","SWEPT_EDGE",EDGE,{"disambiguationData":[OSD([sQuery(id+"F0.wireOp",EDGE,"E0.top"),sQuery(id+"F0.wireOp",EDGE,"E2.1.0.1"),sQuery(id+"F0.wireOp",EDGE,"E2.1.0.3")])]});
            var Q145;
            Q145=makeQuery(id+"F1.opExtrude","CAP_EDGE",EDGE,{"disambiguationData":[OSD([sQuery(id+"F0.wireOp",EDGE,"E2.3.0.1")])],"isStart":false});
            var Q146;
            Q146=makeQuery(id+"F1.opExtrude","SWEPT_EDGE",EDGE,{"disambiguationData":[OSD([sQuery(id+"F0.wireOp",EDGE,"E0.top"),sQuery(id+"F0.wireOp",EDGE,"E2.3.0.1"),sQuery(id+"F0.wireOp",EDGE,"E2.3.0.2")])]});
            var Q147;
            Q147=makeQuery(id+"F1.opExtrude","CAP_EDGE",EDGE,{"disambiguationData":[OSD([sQuery(id+"F0.wireOp",EDGE,"E2.3.0.0")])],"isStart":false});
            var Q148;
            Q148=makeQuery(id+"F1.opExtrude","SWEPT_EDGE",EDGE,{"disambiguationData":[OSD([sQuery(id+"F0.wireOp",EDGE,"E2.3.0.0"),sQuery(id+"F0.wireOp",EDGE,"E2.3.0.2")])]});
            var Q149;
            Q149=makeQuery(id+"F1.opExtrude","SWEPT_EDGE",EDGE,{"disambiguationData":[OSD([sQuery(id+"F0.wireOp",EDGE,"E2.3.0.0"),sQuery(id+"F0.wireOp",EDGE,"E2.3.0.3")])]});
            var Q150;
            Q150=makeQuery(id+"F1.opExtrude","SWEPT_EDGE",EDGE,{"disambiguationData":[OSD([sQuery(id+"F0.wireOp",EDGE,"E0.top"),sQuery(id+"F0.wireOp",EDGE,"E2.3.0.1"),sQuery(id+"F0.wireOp",EDGE,"E2.3.0.3")])]});
            var Q151;
            Q151=makeQuery(id+"F1.opExtrude","SWEPT_EDGE",EDGE,{"disambiguationData":[OSD([sQuery(id+"F0.wireOp",EDGE,"E0.top"),sQuery(id+"F0.wireOp",EDGE,"E2.4.0.1"),sQuery(id+"F0.wireOp",EDGE,"E2.4.0.3")])]});
            var Q152;
            Q152=makeQuery(id+"F1.opExtrude","CAP_EDGE",EDGE,{"disambiguationData":[OSD([sQuery(id+"F0.wireOp",EDGE,"E2.4.0.0")])],"isStart":false});
            var Q153;
            Q153=makeQuery(id+"F1.opExtrude","SWEPT_EDGE",EDGE,{"disambiguationData":[OSD([sQuery(id+"F0.wireOp",EDGE,"E0.top"),sQuery(id+"F0.wireOp",EDGE,"E2.4.0.1"),sQuery(id+"F0.wireOp",EDGE,"E2.4.0.2")])]});
            var Q154;
            Q154=makeQuery(id+"F1.opExtrude","CAP_EDGE",EDGE,{"disambiguationData":[OSD([sQuery(id+"F0.wireOp",EDGE,"E2.4.0.3")])],"isStart":false});
            var Q155;
            Q155=makeQuery(id+"F1.opExtrude","SWEPT_EDGE",EDGE,{"disambiguationData":[OSD([sQuery(id+"F0.wireOp",EDGE,"E2.4.0.0"),sQuery(id+"F0.wireOp",EDGE,"E2.4.0.2")])]});
            var Q156;
            Q156=makeQuery(id+"F1.opExtrude","SWEPT_EDGE",EDGE,{"disambiguationData":[OSD([sQuery(id+"F0.wireOp",EDGE,"E2.4.0.0"),sQuery(id+"F0.wireOp",EDGE,"E2.4.0.3")])]});
            var Q157;
            Q157=makeQuery(id+"F1.opExtrude","CAP_EDGE",EDGE,{"disambiguationData":[OSD([sQuery(id+"F0.wireOp",EDGE,"E2.5.0.0")])],"isStart":true});
            var Q158;
            Q158=makeQuery(id+"F1.opExtrude","SWEPT_EDGE",EDGE,{"disambiguationData":[OSD([sQuery(id+"F0.wireOp",EDGE,"E2.5.0.0"),sQuery(id+"F0.wireOp",EDGE,"E2.5.0.2")])]});
            var Q159;
            Q159=makeQuery(id+"F1.opExtrude","CAP_EDGE",EDGE,{"disambiguationData":[OSD([sQuery(id+"F0.wireOp",EDGE,"E2.5.0.1")])],"isStart":false});
            var Q160;
            Q160=makeQuery(id+"F1.opExtrude","CAP_EDGE",EDGE,{"disambiguationData":[OSD([sQuery(id+"F0.wireOp",EDGE,"E2.5.0.2")])],"isStart":true});
            var Q161;
            Q161=makeQuery(id+"F1.opExtrude","SWEPT_EDGE",EDGE,{"disambiguationData":[OSD([sQuery(id+"F0.wireOp",EDGE,"E2.5.0.0"),sQuery(id+"F0.wireOp",EDGE,"E2.5.0.3")])]});
            var Q162;
            Q162=makeQuery(id+"F1.opExtrude","CAP_EDGE",EDGE,{"disambiguationData":[OSD([sQuery(id+"F0.wireOp",EDGE,"E2.5.0.0")])],"isStart":false});
            var Q163;
            Q163=makeQuery(id+"F1.opExtrude","SWEPT_EDGE",EDGE,{"disambiguationData":[OSD([sQuery(id+"F0.wireOp",EDGE,"E0.top"),sQuery(id+"F0.wireOp",EDGE,"E2.5.0.1"),sQuery(id+"F0.wireOp",EDGE,"E2.5.0.2")])]});
            var Q164;
            Q164=makeQuery(id+"F1.opExtrude","SWEPT_EDGE",EDGE,{"disambiguationData":[OSD([sQuery(id+"F0.wireOp",EDGE,"E0.top"),sQuery(id+"F0.wireOp",EDGE,"E2.5.0.1"),sQuery(id+"F0.wireOp",EDGE,"E2.5.0.3")])]});
            var Q165;
            Q165=makeQuery(id+"F1.opExtrude","SWEPT_EDGE",EDGE,{"disambiguationData":[OSD([sQuery(id+"F0.wireOp",EDGE,"E0.top"),sQuery(id+"F0.wireOp",EDGE,"E2.6.0.1"),sQuery(id+"F0.wireOp",EDGE,"E2.6.0.2")])]});
            var Q166;
            Q166=makeQuery(id+"F1.opExtrude","SWEPT_EDGE",EDGE,{"disambiguationData":[OSD([sQuery(id+"F0.wireOp",EDGE,"E0.top"),sQuery(id+"F0.wireOp",EDGE,"E2.6.0.1"),sQuery(id+"F0.wireOp",EDGE,"E2.6.0.3")])]});
            var Q167;
            Q167=makeQuery(id+"F1.opExtrude","SWEPT_EDGE",EDGE,{"disambiguationData":[OSD([sQuery(id+"F0.wireOp",EDGE,"E2.6.0.0"),sQuery(id+"F0.wireOp",EDGE,"E2.6.0.3")])]});
            var Q168;
            Q168=makeQuery(id+"F1.opExtrude","CAP_EDGE",EDGE,{"disambiguationData":[OSD([sQuery(id+"F0.wireOp",EDGE,"E2.6.0.1")])],"isStart":false});
            var Q169;
            Q169=makeQuery(id+"F1.opExtrude","SWEPT_EDGE",EDGE,{"disambiguationData":[OSD([sQuery(id+"F0.wireOp",EDGE,"E2.6.0.0"),sQuery(id+"F0.wireOp",EDGE,"E2.6.0.2")])]});
            var Q170;
            Q170=makeQuery(id+"F1.opExtrude","CAP_EDGE",EDGE,{"disambiguationData":[OSD([sQuery(id+"F0.wireOp",EDGE,"E2.7.0.0")])],"isStart":true});
            var Q171;
            Q171=makeQuery(id+"F1.opExtrude","SWEPT_EDGE",EDGE,{"disambiguationData":[OSD([sQuery(id+"F0.wireOp",EDGE,"E0.top"),sQuery(id+"F0.wireOp",EDGE,"E2.7.0.1"),sQuery(id+"F0.wireOp",EDGE,"E2.7.0.2")])]});
            var Q172;
            Q172=makeQuery(id+"F1.opExtrude","SWEPT_EDGE",EDGE,{"disambiguationData":[OSD([sQuery(id+"F0.wireOp",EDGE,"E2.7.0.0"),sQuery(id+"F0.wireOp",EDGE,"E2.7.0.3")])]});
            var Q173;
            Q173=makeQuery(id+"F1.opExtrude","SWEPT_EDGE",EDGE,{"disambiguationData":[OSD([sQuery(id+"F0.wireOp",EDGE,"E2.7.0.0"),sQuery(id+"F0.wireOp",EDGE,"E2.7.0.2")])]});
            var Q174;
            Q174=makeQuery(id+"F1.opExtrude","CAP_EDGE",EDGE,{"disambiguationData":[OSD([sQuery(id+"F0.wireOp",EDGE,"E2.7.0.2")])],"isStart":true});
            var Q175;
            Q175=makeQuery(id+"F1.opExtrude","SWEPT_EDGE",EDGE,{"disambiguationData":[OSD([sQuery(id+"F0.wireOp",EDGE,"E0.top"),sQuery(id+"F0.wireOp",EDGE,"E2.7.0.1"),sQuery(id+"F0.wireOp",EDGE,"E2.7.0.3")])]});
            var Q176;
            Q176=makeQuery(id+"F1.opExtrude","CAP_EDGE",EDGE,{"disambiguationData":[OSD([sQuery(id+"F0.wireOp",EDGE,"E3.0.8.0")])],"isStart":false});
            var Q177;
            Q177=makeQuery(id+"F1.opExtrude","CAP_EDGE",EDGE,{"disambiguationData":[OSD([sQuery(id+"F0.wireOp",EDGE,"E3.0.8.0")])],"isStart":true});
            var Q178;
            Q178=makeQuery(id+"F1.opExtrude","SWEPT_EDGE",EDGE,{"disambiguationData":[OSD([sQuery(id+"F0.wireOp",EDGE,"E0.top"),sQuery(id+"F0.wireOp",EDGE,"E3.3.8.0"),sQuery(id+"F0.wireOp",EDGE,"E3.6.8.0")])]});
            var Q179;
            Q179=makeQuery(id+"F1.opExtrude","SWEPT_EDGE",EDGE,{"disambiguationData":[OSD([sQuery(id+"F0.wireOp",EDGE,"E3.0.8.0"),sQuery(id+"F0.wireOp",EDGE,"E3.6.8.0")])]});
            var Q180;
            Q180=makeQuery(id+"F1.opExtrude","CAP_EDGE",EDGE,{"disambiguationData":[OSD([sQuery(id+"F0.wireOp",EDGE,"E3.9.8.0")])],"isStart":true});
            var Q181;
            Q181=makeQuery(id+"F1.opExtrude","CAP_EDGE",EDGE,{"disambiguationData":[OSD([sQuery(id+"F0.wireOp",EDGE,"E4.left")])],"isStart":true});
            var Q182;
            Q182=makeQuery(id+"F1.opExtrude","CAP_EDGE",EDGE,{"disambiguationData":[OSD([sQuery(id+"F0.wireOp",EDGE,"E4.bottom")])],"isStart":true});
            var Q183;
            Q183=makeQuery(id+"F1.opExtrude","CAP_EDGE",EDGE,{"disambiguationData":[OSD([sQuery(id+"F0.wireOp",EDGE,"E4.bottom")])],"isStart":false});
            var Q184;
            Q184=makeQuery(id+"F1.opExtrude","CAP_EDGE",EDGE,{"disambiguationData":[OSD([sQuery(id+"F0.wireOp",EDGE,"E4.left")])],"isStart":false});
            var Q185;
            Q185=makeQuery(id+"F1.opExtrude","CAP_EDGE",EDGE,{"disambiguationData":[OSD([sQuery(id+"F0.wireOp",EDGE,"E4.right")])],"isStart":true});
            var Q186;
            Q186=makeQuery(id+"F1.opExtrude","CAP_EDGE",EDGE,{"disambiguationData":[OSD([sQuery(id+"F0.wireOp",EDGE,"E4.right")])],"isStart":false});
            var Q187;
            Q187=makeQuery(id+"F1.opExtrude","CAP_EDGE",EDGE,{"disambiguationData":[OSD([sQuery(id+"F0.wireOp",EDGE,"E5.1.0.0")])],"isStart":false});
            var Q188;
            Q188=makeQuery(id+"F1.opExtrude","CAP_EDGE",EDGE,{"disambiguationData":[OSD([sQuery(id+"F0.wireOp",EDGE,"E5.1.0.1")])],"isStart":true});
            var Q189;
            Q189=makeQuery(id+"F1.opExtrude","CAP_EDGE",EDGE,{"disambiguationData":[OSD([sQuery(id+"F0.wireOp",EDGE,"E5.1.0.1")])],"isStart":false});
            var Q190;
            Q190=makeQuery(id+"F1.opExtrude","CAP_EDGE",EDGE,{"disambiguationData":[OSD([sQuery(id+"F0.wireOp",EDGE,"E5.1.0.2")])],"isStart":false});
            var Q191;
            Q191=makeQuery(id+"F1.opExtrude","CAP_EDGE",EDGE,{"disambiguationData":[OSD([sQuery(id+"F0.wireOp",EDGE,"E5.2.0.1")])],"isStart":true});
            var Q192;
            Q192=makeQuery(id+"F1.opExtrude","CAP_EDGE",EDGE,{"disambiguationData":[OSD([sQuery(id+"F0.wireOp",EDGE,"E5.3.0.1")])],"isStart":false});
            var Q193;
            Q193=makeQuery(id+"F1.opExtrude","CAP_EDGE",EDGE,{"disambiguationData":[OSD([sQuery(id+"F0.wireOp",EDGE,"E5.5.0.1")])],"isStart":false});
            var Q194;
            Q194=makeQuery(id+"F1.opExtrude","CAP_EDGE",EDGE,{"disambiguationData":[OSD([sQuery(id+"F0.wireOp",EDGE,"E5.6.0.1")])],"isStart":false});
            var Q195;
            Q195=makeQuery(id+"F1.opExtrude","CAP_EDGE",EDGE,{"disambiguationData":[OSD([sQuery(id+"F0.wireOp",EDGE,"E5.7.0.1")])],"isStart":true});
            var Q196;
            Q196=makeQuery(id+"F1.opExtrude","CAP_EDGE",EDGE,{"disambiguationData":[OSD([sQuery(id+"F0.wireOp",EDGE,"E5.7.0.1")])],"isStart":false});
            var Q197;
            Q197=makeQuery(id+"F1.opExtrude","CAP_EDGE",EDGE,{"disambiguationData":[OSD([sQuery(id+"F0.wireOp",EDGE,"E5.7.0.2")])],"isStart":false});
            var Q198;
            Q198=makeQuery(id+"F3.opExtrude","CAP_EDGE",EDGE,{"disambiguationData":[OSD([sQuery(id+"F2.wireOp",EDGE,"E6.top")])],"isStart":false});
            var Q199;
            Q199=makeQuery(id+"F3.opExtrude","CAP_EDGE",EDGE,{"disambiguationData":[OSD([sQuery(id+"F2.wireOp",EDGE,"E6.bottom")])],"isStart":false});
            var Q200;
            Q200=makeQuery(id+"F3.opExtrude","CAP_EDGE",EDGE,{"disambiguationData":[OSD([sQuery(id+"F2.wireOp",EDGE,"E6.right")])],"isStart":false});
            var Q201;
            Q201=makeQuery(id+"F3.opExtrude","CAP_EDGE",EDGE,{"disambiguationData":[OSD([sQuery(id+"F2.wireOp",EDGE,"E7.top")])],"isStart":false});
            var Q202;
            Q202=makeQuery(id+"F3.opExtrude","CAP_EDGE",EDGE,{"disambiguationData":[OSD([sQuery(id+"F2.wireOp",EDGE,"E7.bottom")])],"isStart":false});
            var Q203;
            Q203=makeQuery(id+"F5.opExtrude","CAP_EDGE",EDGE,{"disambiguationData":[OSD([sQuery(id+"F4.wireOp",EDGE,"E8.left")])],"isStart":true});
            var Q204;
            Q204=makeQuery(id+"F5.opExtrude","CAP_EDGE",EDGE,{"disambiguationData":[OSD([sQuery(id+"F4.wireOp",EDGE,"E8.bottom")])],"isStart":true});
            var Q205;
            Q205=makeQuery(id+"F5.opExtrude","SWEPT_EDGE",EDGE,{"disambiguationData":[OSD([sQuery(id+"F4.wireOp",EDGE,"E8.bottom"),sQuery(id+"F4.wireOp",EDGE,"E8.right")])]});
            var Q206;
            Q206=makeQuery(id+"F5.opExtrude","CAP_EDGE",EDGE,{"disambiguationData":[OSD([sQuery(id+"F4.wireOp",EDGE,"E8.right")])],"isStart":true});
            var Q207;
            Q207=makeQuery(id+"F1.opExtrude","CAP_EDGE",EDGE,{"disambiguationData":[OSD([sQuery(id+"F0.wireOp",EDGE,"E2.2.0.1")])],"isStart":false});
            var Q208;
            Q208=makeQuery(id+"F1.opExtrude","CAP_EDGE",EDGE,{"disambiguationData":[OSD([sQuery(id+"F0.wireOp",EDGE,"E2.2.0.0")])],"isStart":true});
            var Q209;
            Q209=makeQuery(id+"F1.opExtrude","CAP_EDGE",EDGE,{"disambiguationData":[OSD([sQuery(id+"F0.wireOp",EDGE,"E2.2.0.2")])],"isStart":true});
            var Q210;
            Q210=makeQuery(id+"F1.opExtrude","CAP_EDGE",EDGE,{"disambiguationData":[OSD([sQuery(id+"F0.wireOp",EDGE,"E2.2.0.3")])],"isStart":true});
            var Q211;
            Q211=makeQuery(id+"F1.opExtrude","CAP_EDGE",EDGE,{"disambiguationData":[OSD([sQuery(id+"F0.wireOp",EDGE,"E1.top")])],"isStart":true});
            var Q212;
            Q212=makeQuery(id+"F1.opExtrude","CAP_EDGE",EDGE,{"disambiguationData":[OSD([sQuery(id+"F0.wireOp",EDGE,"E1.left")])],"isStart":true});
            var Q213;
            Q213=makeQuery(id+"F1.opExtrude","CAP_EDGE",EDGE,{"disambiguationData":[OSD([sQuery(id+"F0.wireOp",EDGE,"E2.1.0.1")])],"isStart":true});
            var Q214;
            Q214=makeQuery(id+"F1.opExtrude","CAP_EDGE",EDGE,{"disambiguationData":[OSD([sQuery(id+"F0.wireOp",EDGE,"E2.1.0.0")])],"isStart":true});
            var Q215;
            Q215=makeQuery(id+"F1.opExtrude","CAP_EDGE",EDGE,{"disambiguationData":[OSD([sQuery(id+"F0.wireOp",EDGE,"E2.1.0.2")])],"isStart":false});
            var Q216;
            Q216=makeQuery(id+"F1.opExtrude","CAP_EDGE",EDGE,{"disambiguationData":[OSD([sQuery(id+"F0.wireOp",EDGE,"E2.1.0.3")])],"isStart":false});
            var Q217;
            Q217=makeQuery(id+"F1.opExtrude","CAP_EDGE",EDGE,{"disambiguationData":[OSD([sQuery(id+"F0.wireOp",EDGE,"E2.3.0.1")])],"isStart":true});
            var Q218;
            Q218=makeQuery(id+"F1.opExtrude","CAP_EDGE",EDGE,{"disambiguationData":[OSD([sQuery(id+"F0.wireOp",EDGE,"E2.3.0.0")])],"isStart":true});
            var Q219;
            Q219=makeQuery(id+"F1.opExtrude","CAP_EDGE",EDGE,{"disambiguationData":[OSD([sQuery(id+"F0.wireOp",EDGE,"E2.3.0.2")])],"isStart":false});
            var Q220;
            Q220=makeQuery(id+"F1.opExtrude","CAP_EDGE",EDGE,{"disambiguationData":[OSD([sQuery(id+"F0.wireOp",EDGE,"E2.3.0.3")])],"isStart":false});
            var Q221;
            Q221=makeQuery(id+"F1.opExtrude","CAP_EDGE",EDGE,{"disambiguationData":[OSD([sQuery(id+"F0.wireOp",EDGE,"E2.4.0.1")])],"isStart":true});
            var Q222;
            Q222=makeQuery(id+"F1.opExtrude","CAP_EDGE",EDGE,{"disambiguationData":[OSD([sQuery(id+"F0.wireOp",EDGE,"E2.4.0.0")])],"isStart":true});
            var Q223;
            Q223=makeQuery(id+"F1.opExtrude","CAP_EDGE",EDGE,{"disambiguationData":[OSD([sQuery(id+"F0.wireOp",EDGE,"E2.4.0.1")])],"isStart":false});
            var Q224;
            Q224=makeQuery(id+"F1.opExtrude","CAP_EDGE",EDGE,{"disambiguationData":[OSD([sQuery(id+"F0.wireOp",EDGE,"E2.5.0.2")])],"isStart":false});
            var Q225;
            Q225=makeQuery(id+"F1.opExtrude","CAP_EDGE",EDGE,{"disambiguationData":[OSD([sQuery(id+"F0.wireOp",EDGE,"E2.5.0.3")])],"isStart":true});
            var Q226;
            Q226=makeQuery(id+"F1.opExtrude","CAP_EDGE",EDGE,{"disambiguationData":[OSD([sQuery(id+"F0.wireOp",EDGE,"E2.5.0.3")])],"isStart":false});
            var Q227;
            Q227=makeQuery(id+"F1.opExtrude","CAP_EDGE",EDGE,{"disambiguationData":[OSD([sQuery(id+"F0.wireOp",EDGE,"E2.6.0.1")])],"isStart":true});
            var Q228;
            Q228=makeQuery(id+"F1.opExtrude","CAP_EDGE",EDGE,{"disambiguationData":[OSD([sQuery(id+"F0.wireOp",EDGE,"E2.6.0.0")])],"isStart":false});
            var Q229;
            Q229=makeQuery(id+"F1.opExtrude","CAP_EDGE",EDGE,{"disambiguationData":[OSD([sQuery(id+"F0.wireOp",EDGE,"E2.6.0.0")])],"isStart":true});
            var Q230;
            Q230=makeQuery(id+"F1.opExtrude","CAP_EDGE",EDGE,{"disambiguationData":[OSD([sQuery(id+"F0.wireOp",EDGE,"E2.6.0.3")])],"isStart":false});
            var Q231;
            Q231=makeQuery(id+"F1.opExtrude","CAP_EDGE",EDGE,{"disambiguationData":[OSD([sQuery(id+"F0.wireOp",EDGE,"E2.6.0.2")])],"isStart":false});
            var Q232;
            Q232=makeQuery(id+"F1.opExtrude","CAP_EDGE",EDGE,{"disambiguationData":[OSD([sQuery(id+"F0.wireOp",EDGE,"E2.7.0.1")])],"isStart":false});
            var Q233;
            Q233=makeQuery(id+"F1.opExtrude","CAP_EDGE",EDGE,{"disambiguationData":[OSD([sQuery(id+"F0.wireOp",EDGE,"E2.7.0.0")])],"isStart":false});
            var Q234;
            Q234=makeQuery(id+"F1.opExtrude","CAP_EDGE",EDGE,{"disambiguationData":[OSD([sQuery(id+"F0.wireOp",EDGE,"E2.7.0.3")])],"isStart":true});
            var Q235;
            Q235=makeQuery(id+"F1.opExtrude","CAP_EDGE",EDGE,{"disambiguationData":[OSD([sQuery(id+"F0.wireOp",EDGE,"E3.6.8.0")])],"isStart":true});
            var Q236;
            Q236=makeQuery(id+"F1.opExtrude","CAP_EDGE",EDGE,{"disambiguationData":[OSD([sQuery(id+"F0.wireOp",EDGE,"E3.6.8.0")])],"isStart":false});
            var Q237;
            Q237=makeQuery(id+"F3.opExtrude","CAP_EDGE",EDGE,{"disambiguationData":[OSD([sQuery(id+"F2.wireOp",EDGE,"E6.right")])],"isStart":true});
            var Q238;
            Q238=makeQuery(id+"F3.opExtrude","CAP_EDGE",EDGE,{"disambiguationData":[OSD([sQuery(id+"F2.wireOp",EDGE,"E7.right")])],"isStart":false});
            var Q239;
            Q239=makeQuery(id+"F3.opExtrude","CAP_EDGE",EDGE,{"disambiguationData":[OSD([sQuery(id+"F2.wireOp",EDGE,"E7.right")])],"isStart":true});
            var Q240;
            Q240=makeQuery(id+"F1.opExtrude","CAP_EDGE",EDGE,{"disambiguationData":[OSD([sQuery(id+"F0.wireOp",EDGE,"E2.2.0.2")])],"isStart":false});
            var Q241;
            Q241=makeQuery(id+"F1.opExtrude","CAP_EDGE",EDGE,{"disambiguationData":[OSD([sQuery(id+"F0.wireOp",EDGE,"E1.right")])],"isStart":true});
            var Q242;
            Q242=makeQuery(id+"F1.opExtrude","CAP_EDGE",EDGE,{"disambiguationData":[OSD([sQuery(id+"F0.wireOp",EDGE,"E2.1.0.2")])],"isStart":true});
            var Q243;
            Q243=makeQuery(id+"F1.opExtrude","CAP_EDGE",EDGE,{"disambiguationData":[OSD([sQuery(id+"F0.wireOp",EDGE,"E2.1.0.3")])],"isStart":true});
            var Q244;
            Q244=makeQuery(id+"F1.opExtrude","CAP_EDGE",EDGE,{"disambiguationData":[OSD([sQuery(id+"F0.wireOp",EDGE,"E2.3.0.2")])],"isStart":true});
            var Q245;
            Q245=makeQuery(id+"F1.opExtrude","CAP_EDGE",EDGE,{"disambiguationData":[OSD([sQuery(id+"F0.wireOp",EDGE,"E2.3.0.3")])],"isStart":true});
            var Q246;
            Q246=makeQuery(id+"F1.opExtrude","CAP_EDGE",EDGE,{"disambiguationData":[OSD([sQuery(id+"F0.wireOp",EDGE,"E2.4.0.2")])],"isStart":true});
            var Q247;
            Q247=makeQuery(id+"F1.opExtrude","CAP_EDGE",EDGE,{"disambiguationData":[OSD([sQuery(id+"F0.wireOp",EDGE,"E2.4.0.2")])],"isStart":false});
            var Q248;
            Q248=makeQuery(id+"F1.opExtrude","CAP_EDGE",EDGE,{"disambiguationData":[OSD([sQuery(id+"F0.wireOp",EDGE,"E2.4.0.3")])],"isStart":true});
            var Q249;
            Q249=makeQuery(id+"F1.opExtrude","CAP_EDGE",EDGE,{"disambiguationData":[OSD([sQuery(id+"F0.wireOp",EDGE,"E2.6.0.2")])],"isStart":true});
            var Q250;
            Q250=makeQuery(id+"F1.opExtrude","CAP_EDGE",EDGE,{"disambiguationData":[OSD([sQuery(id+"F0.wireOp",EDGE,"E2.6.0.3")])],"isStart":true});
            var Q251;
            Q251=makeQuery(id+"F1.opExtrude","CAP_EDGE",EDGE,{"disambiguationData":[OSD([sQuery(id+"F0.wireOp",EDGE,"E2.7.0.2")])],"isStart":false});
            var Q252;
            Q252=makeQuery(id+"F1.opExtrude","CAP_EDGE",EDGE,{"disambiguationData":[OSD([sQuery(id+"F0.wireOp",EDGE,"E2.7.0.3")])],"isStart":false});
            fillet(context, id + "F6", {"entities" : qUnion([Q0, Q1, Q2, Q3, Q4, Q5, Q6, Q7, Q8, Q9, Q10, Q11, Q12, Q13, Q14, Q15, Q16, Q17, Q18, Q19, Q20, Q21, Q22, Q23, Q24, Q25, Q26, Q27, Q28, Q29, Q30, Q31, Q32, Q33, Q34, Q35, Q36, Q37, Q38, Q39, Q40, Q41, Q42, Q43, Q44, Q45, Q46, Q47, Q48, Q49, Q50, Q51, Q52, Q53, Q54, Q55, Q56, Q57, Q58, Q59, Q60, Q61, Q62, Q63, Q64, Q65, Q66, Q67, Q68, Q69, Q70, Q71, Q72, Q73, Q74, Q75, Q76, Q77, Q78, Q79, Q80, Q81, Q82, Q83, Q84, Q85, Q86, Q87, Q88, Q89, Q90, Q91, Q92, Q93, Q94, Q95, Q96, Q97, Q98, Q99, Q100, Q101, Q102, Q103, Q104, Q105, Q106, Q107, Q108, Q109, Q110, Q111, Q112, Q113, Q114, Q115, Q116, Q117, Q118, Q119, Q120, Q121, Q122, Q123, Q124, Q125, Q126, Q127, Q128, Q129, Q130, Q131, Q132, Q133, Q134, Q135, Q136, Q137, Q138, Q139, Q140, Q141, Q142, Q143, Q144, Q145, Q146, Q147, Q148, Q149, Q150, Q151, Q152, Q153, Q154, Q155, Q156, Q157, Q158, Q159, Q160, Q161, Q162, Q163, Q164, Q165, Q166, Q167, Q168, Q169, Q170, Q171, Q172, Q173, Q174, Q175, Q176, Q177, Q178, Q179, Q180, Q181, Q182, Q183, Q184, Q185, Q186, Q187, Q188, Q189, Q190, Q191, Q192, Q193, Q194, Q195, Q196, Q197, Q198, Q199, Q200, Q201, Q202, Q203, Q204, Q205, Q206, Q207, Q208, Q209, Q210, Q211, Q212, Q213, Q214, Q215, Q216, Q217, Q218, Q219, Q220, Q221, Q222, Q223, Q224, Q225, Q226, Q227, Q228, Q229, Q230, Q231, Q232, Q233, Q234, Q235, Q236, Q237, Q238, Q239, Q240, Q241, Q242, Q243, Q244, Q245, Q246, Q247, Q248, Q249, Q250, Q251, Q252]), "radius" : 5 * mm, "tangentPropagation" : true, "allowEdgeOverflow" : false});
        }
    });
